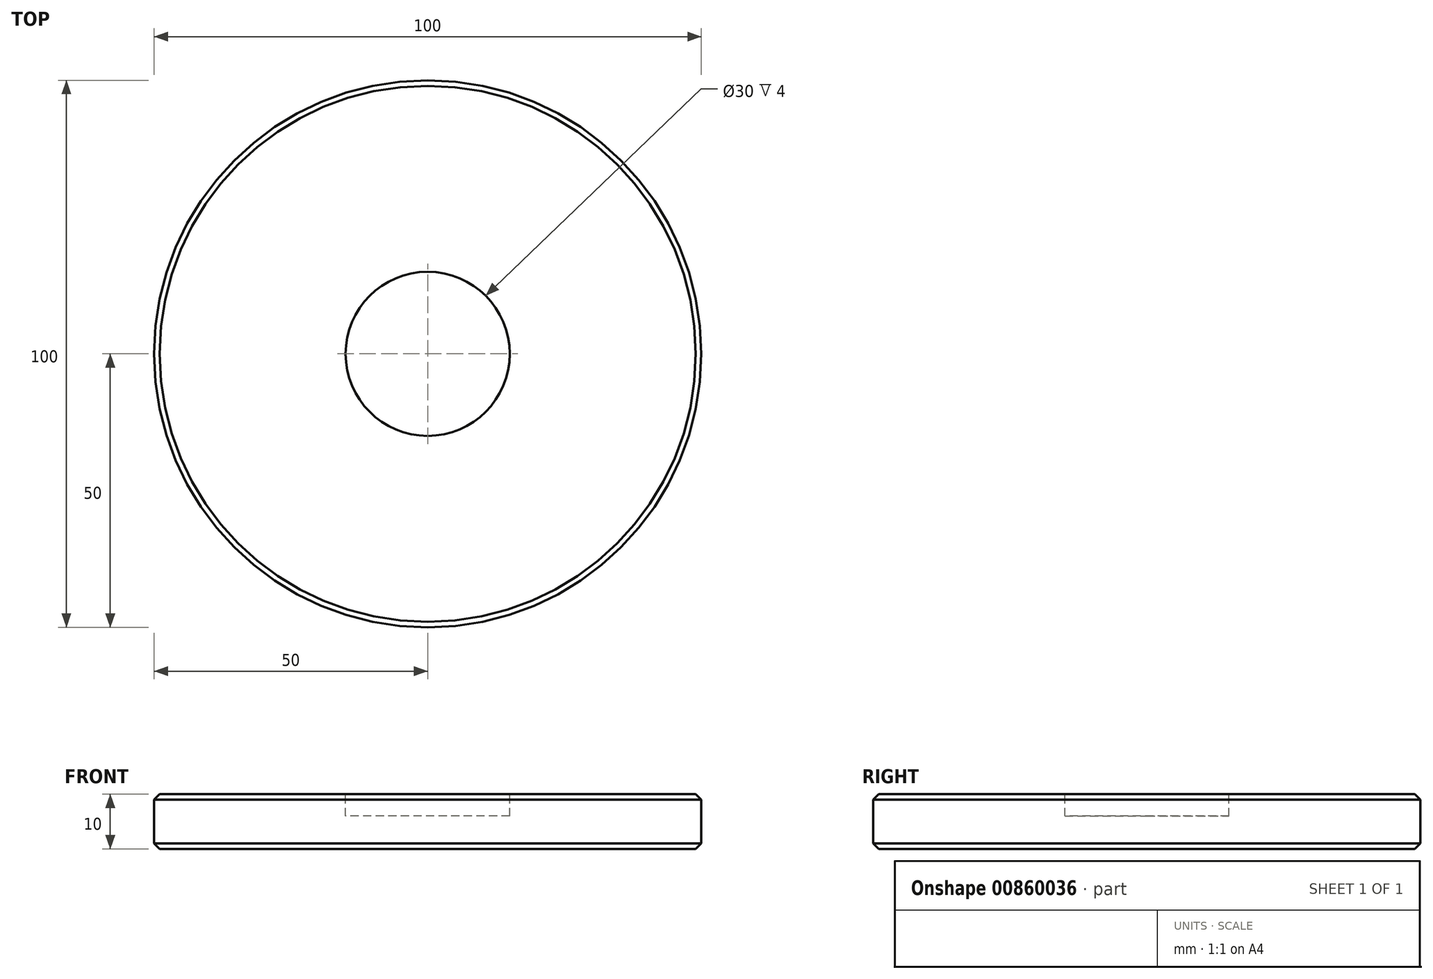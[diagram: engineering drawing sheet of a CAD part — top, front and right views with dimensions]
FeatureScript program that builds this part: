
annotation { "Feature Type Name" : "Feature", "Feature Type Description" : "" }
export const myFeature = defineFeature(function(context is Context, id is Id, definition is map)
    precondition{}
    {
        {
            var Q0;
            Q0=qCreatedBy(makeId("Top.planeOp"),FACE);
            var sketch = newSketch(context, id + "F0", { "sketchPlane" : qUnion([Q0])});
            skCircle(sketch, "E0", {"center": v(0, 0) * mm, "radius": 50 * mm});
            skSolve(sketch);
        }
        {
            var Q0;
            Q0=makeQuery(id+"F0.imprint","IMPRINT",FACE,{"disambiguationData":[TD([[makeQuery(id+"F0.imprint","IMPRINT",EDGE,{"derivedFrom":sQuery(id+"F0.wireOp",EDGE,"E0")}),1.0]])]});
            extrude(context, id + "F1", {"entities" : qUnion([Q0]), "depth" : 10 * mm, "offsetDistance" : 25 * mm});
        }
        {
            var Q0;
            Q0=makeQuery(id+"F1.opExtrude","CAP_FACE",FACE,{"disambiguationData":[OSD([sQuery(id+"F0.wireOp",EDGE,"E0")])],"isStart":false});
            var sketch = newSketch(context, id + "F2", { "sketchPlane" : qUnion([Q0])});
            skCircle(sketch, "E1", {"center": v(0, 0) * mm, "radius": 15 * mm});
            skSolve(sketch);
        }
        {
            var Q0;
            Q0=qSketchRegion(id+"F2",true);
            extrude(context, id + "F3", {"entities" : qUnion([Q0]), "operationType" : NewBodyOperationType.REMOVE, "oppositeDirection" : true, "depth" : 4 * mm, "offsetDistance" : 25 * mm});
        }
        {
            var Q0;
            Q0=makeQuery(id+"F1.opExtrude","CAP_EDGE",EDGE,{"disambiguationData":[OSD([sQuery(id+"F0.wireOp",EDGE,"E0")])],"isStart":false});
            var Q1;
            Q1=makeQuery(id+"F1.opExtrude","CAP_EDGE",EDGE,{"disambiguationData":[OSD([sQuery(id+"F0.wireOp",EDGE,"E0")])],"isStart":true});
            chamfer(context, id + "F4", {"entities" : qUnion([Q0, Q1]), "width" : 1 * mm, "tangentPropagation" : true});
        }
    });
